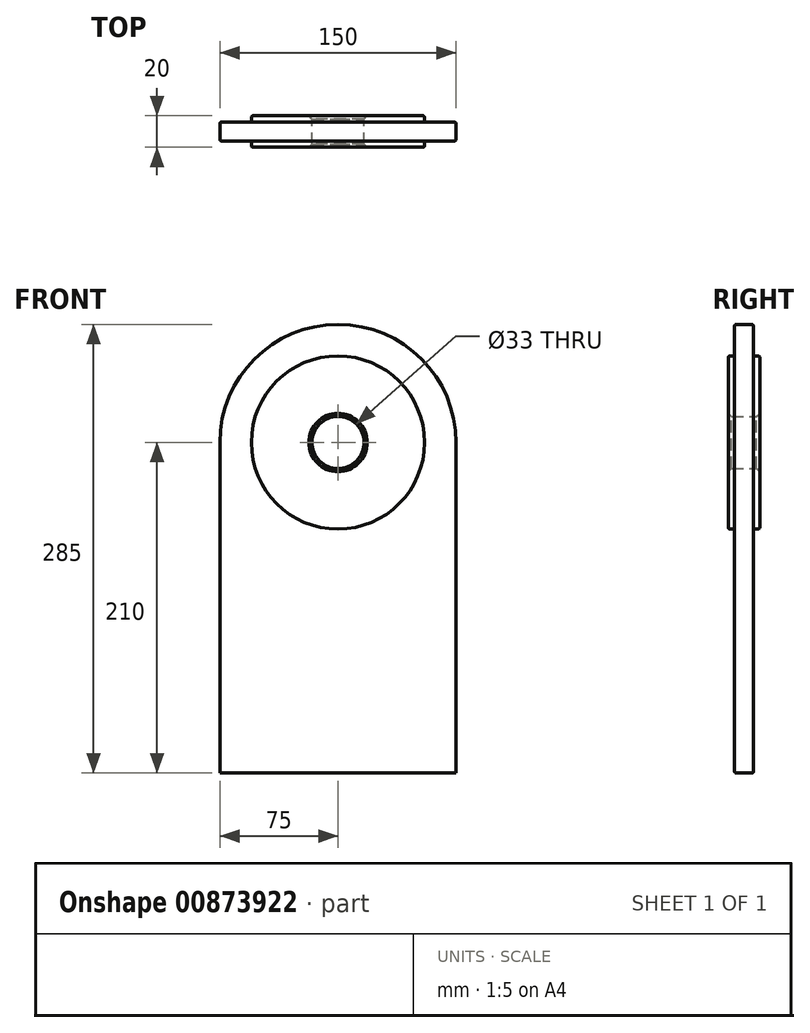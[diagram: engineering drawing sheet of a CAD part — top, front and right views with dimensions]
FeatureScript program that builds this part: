
annotation { "Feature Type Name" : "Feature", "Feature Type Description" : "" }
export const myFeature = defineFeature(function(context is Context, id is Id, definition is map)
    precondition{}
    {
        {
            var Q0;
            Q0=qCreatedBy(makeId("Front.planeOp"),FACE);
            var sketch = newSketch(context, id + "F0", { "sketchPlane" : qUnion([Q0])});
            skArc(sketch, "E0", {"start": v(75, 0) * mm, "mid": v(0, 75) * mm, "end": v(-75, 0) * mm});
            skLineSegment(sketch, "E1.top", {"start": v(-75, -210) * mm, "end": v(75, -210) * mm});
            skLineSegment(sketch, "E1.left", {"start": v(-75, 0) * mm, "end": v(-75, -210) * mm});
            skLineSegment(sketch, "E1.right", {"start": v(75, 0) * mm, "end": v(75, -210) * mm});
            skCircle(sketch, "E2.0", {"center": v(0, 0) * mm, "radius": 55 * mm});
            skCircle(sketch, "E3", {"center": v(0, 0) * mm, "radius": 16.5 * mm});
            skSolve(sketch);
        }
        {
            var Q0;
            Q0=makeQuery(id+"F0.imprint","IMPRINT",FACE,{"disambiguationData":[TD([[makeQuery(id+"F0.imprint","IMPRINT",EDGE,{"derivedFrom":sQuery(id+"F0.wireOp",EDGE,"E0")}),1.0]])]});
            extrude(context, id + "F1", {"entities" : qUnion([Q0]), "depth" : 12 * mm, "offsetDistance" : 25 * mm, "symmetric" : true});
        }
        {
            var Q0;
            Q0=makeQuery(id+"F0.imprint","IMPRINT",FACE,{"disambiguationData":[TD([[makeQuery(id+"F0.imprint","IMPRINT",EDGE,{"derivedFrom":sQuery(id+"F0.wireOp",EDGE,"E2.0")}),1.0]])]});
            extrude(context, id + "F2", {"entities" : qUnion([Q0]), "operationType" : NewBodyOperationType.ADD, "depth" : 20 * mm, "offsetDistance" : 25 * mm, "symmetric" : true});
        }
        {
            var Q0;
            Q0=makeQuery(id+"F2.opExtrude","CAP_EDGE",EDGE,{"disambiguationData":[OSD([sQuery(id+"F0.wireOp",EDGE,"E3")])],"isStart":false});
            var Q1;
            Q1=makeQuery(id+"F2.opExtrude","CAP_EDGE",EDGE,{"disambiguationData":[OSD([sQuery(id+"F0.wireOp",EDGE,"E3")])],"isStart":true});
            chamfer(context, id + "F3", {"entities" : qUnion([Q0, Q1]), "width" : 2 * mm, "tangentPropagation" : true});
        }
        {
            var Q0;
            Q0=makeQuery(id+"F2.opExtrude","CAP_EDGE",EDGE,{"disambiguationData":[OSD([sQuery(id+"F0.wireOp",EDGE,"E2.0")])],"isStart":true});
            var Q1;
            Q1=makeQuery(id+"F1.opExtrude","CAP_FACE",FACE,{"disambiguationData":[OSD([sQuery(id+"F0.wireOp",EDGE,"E0"),sQuery(id+"F0.wireOp",EDGE,"E1.top"),sQuery(id+"F0.wireOp",EDGE,"E1.left"),sQuery(id+"F0.wireOp",EDGE,"E1.right"),sQuery(id+"F0.wireOp",EDGE,"E2.0")])],"isStart":true});
            var Q2;
            Q2=makeQuery(id+"F1.opExtrude","CAP_FACE",FACE,{"disambiguationData":[OSD([sQuery(id+"F0.wireOp",EDGE,"E0"),sQuery(id+"F0.wireOp",EDGE,"E1.top"),sQuery(id+"F0.wireOp",EDGE,"E1.left"),sQuery(id+"F0.wireOp",EDGE,"E1.right"),sQuery(id+"F0.wireOp",EDGE,"E2.0")])],"isStart":false});
            fillet(context, id + "F4", {"entities" : qUnion([Q0, Q1, Q2]), "radius" : 1 * mm, "tangentPropagation" : true, "allowEdgeOverflow" : false});
        }
        {
            var Q0;
            Q0=makeQuery(id+"F2.opExtrude","CAP_EDGE",EDGE,{"disambiguationData":[OSD([sQuery(id+"F0.wireOp",EDGE,"E2.0")])],"isStart":false});
            fillet(context, id + "F5", {"entities" : qUnion([Q0]), "radius" : 1 * mm, "tangentPropagation" : true, "allowEdgeOverflow" : false});
        }
    });
